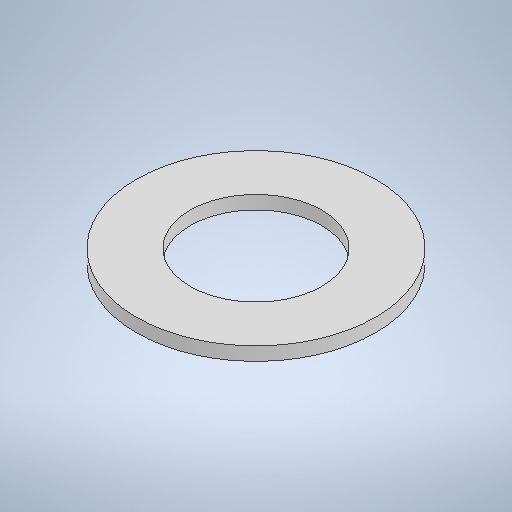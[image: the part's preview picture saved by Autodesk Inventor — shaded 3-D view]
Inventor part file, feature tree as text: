
AUTODESK INVENTOR PART (.ipt)
format: ipt  version: 2025.4 (Build 294407000, 407)  size: 270,336 bytes
history: native  units: mm
features: other x2, sheet_metal_op x1, sketch x1
ambient origin geometry x8: Origin, YZ Plane, XZ Plane, XY Plane, X Axis, Y Axis, Z Axis, Center Point
bodies: Body1 (feature_tree)
feature tree (4):
  sheet_metal_op  "Face2"
  sketch  "Sketch2"  dims[d14=6.0mm d25=59.0mm d29=24.0mm]
  other  "Plate2"
  other  "Definition1"
